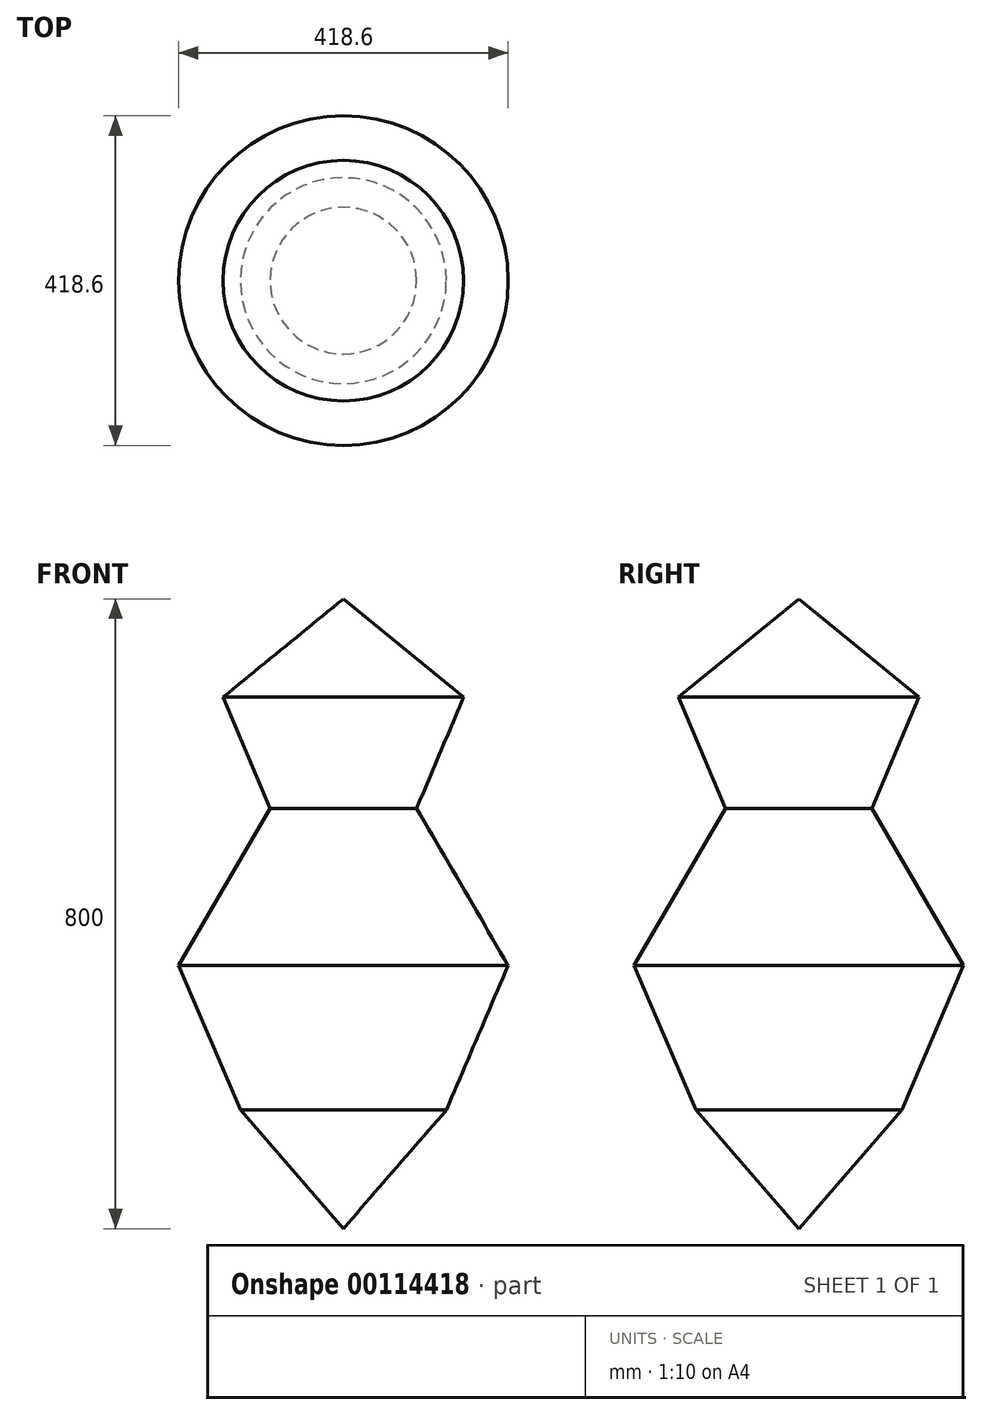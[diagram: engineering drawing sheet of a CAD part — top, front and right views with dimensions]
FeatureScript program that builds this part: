
annotation { "Feature Type Name" : "Feature", "Feature Type Description" : "" }
export const myFeature = defineFeature(function(context is Context, id is Id, definition is map)
    precondition{}
    {
        {
            var Q0;
            Q0=qCreatedBy(makeId("Front.planeOp"),FACE);
            var sketch = newSketch(context, id + "F0", { "sketchPlane" : qUnion([Q0])});
            skLineSegment(sketch, "E0", {"start": v(0, 354.98) * mm, "end": v(0, -445.02) * mm, "construction": true});
            skLineSegment(sketch, "E1", {"start": v(0, 354.98) * mm, "end": v(-152.77, 230.24) * mm});
            skLineSegment(sketch, "E2", {"start": v(-152.77, 230.24) * mm, "end": v(-93.1, 88.9) * mm});
            skLineSegment(sketch, "E3", {"start": v(-93.1, 88.9) * mm, "end": v(-209.3, -110.53) * mm});
            skLineSegment(sketch, "E4", {"start": v(-209.3, -110.53) * mm, "end": v(-130.78, -294.26) * mm});
            skLineSegment(sketch, "E5", {"start": v(-130.78, -294.26) * mm, "end": v(0, -445.02) * mm});
            skLineSegment(sketch, "E6", {"start": v(0, 354.98) * mm, "end": v(0, -445.02) * mm});
            skSolve(sketch);
        }
        {
            var Q0;
            Q0 = qSketchRegion(id + "F0", true);
            var Q1;
            Q1=sQuery(id+"F0.wireOp",EDGE,"E6");
            revolve(context, id + "F1", {"entities" : qUnion([Q0]), "axis" : qUnion([Q1]), "revolveType" : RevolveType.FULL});
        }
    });
